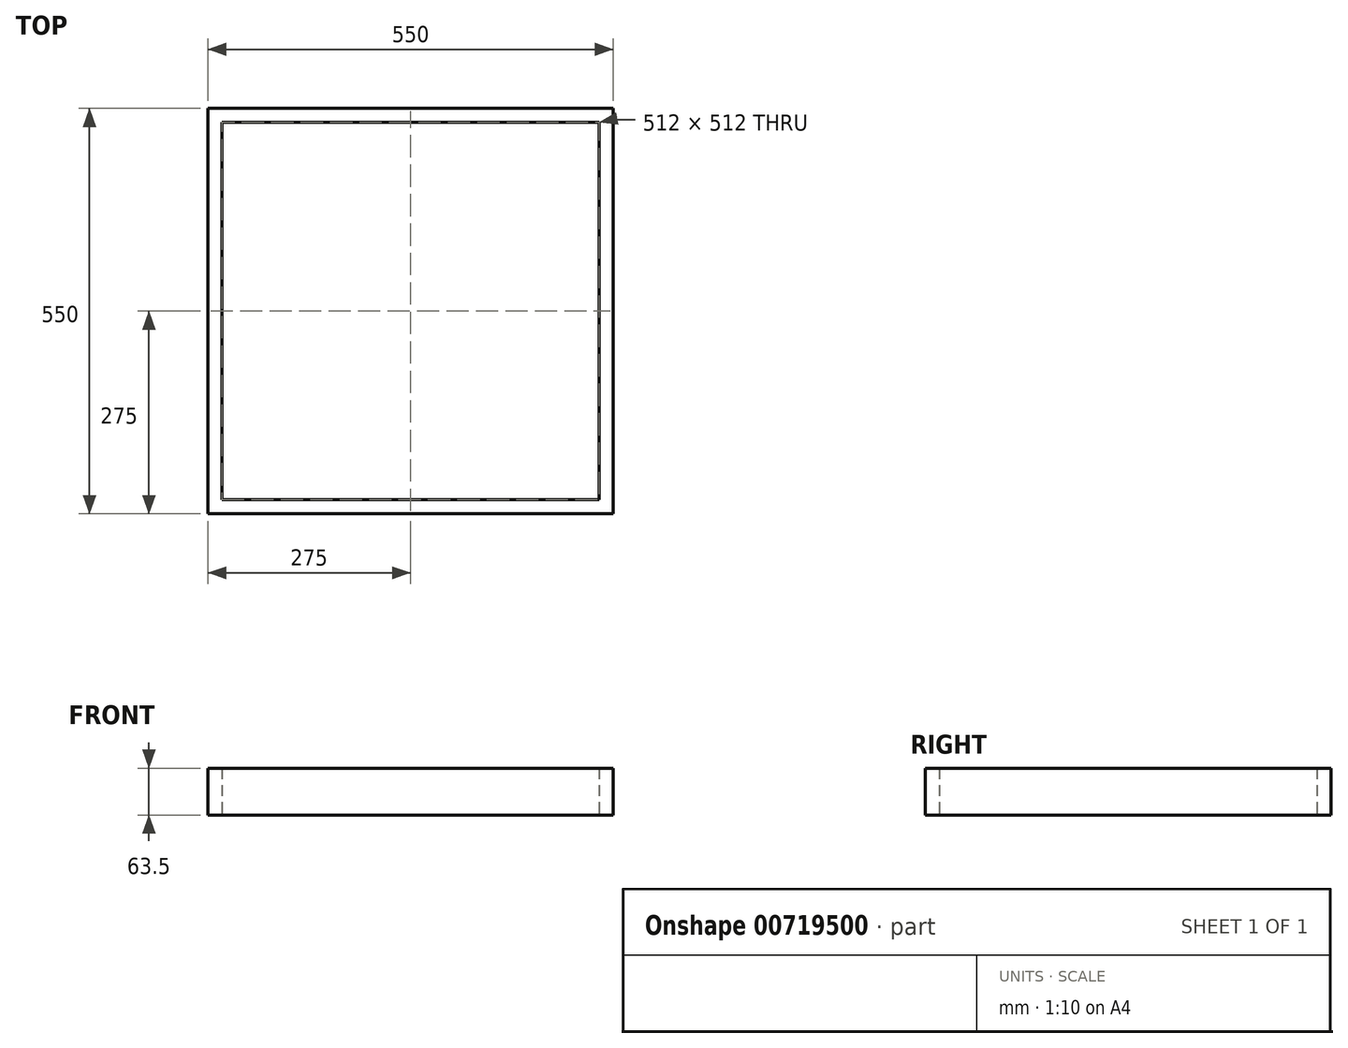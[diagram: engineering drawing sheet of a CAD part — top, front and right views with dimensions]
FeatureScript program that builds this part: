
annotation { "Feature Type Name" : "Feature", "Feature Type Description" : "" }
export const myFeature = defineFeature(function(context is Context, id is Id, definition is map)
    precondition{}
    {
        {
            var Q0;
            Q0=qCreatedBy(makeId("Top.planeOp"),FACE);
            var sketch = newSketch(context, id + "F0", { "sketchPlane" : qUnion([Q0])});
            skLineSegment(sketch, "E0.bottom", {"start": v(275, -275) * mm, "end": v(-275, -275) * mm});
            skLineSegment(sketch, "E0.top", {"start": v(275, 275) * mm, "end": v(-275, 275) * mm});
            skLineSegment(sketch, "E0.left", {"start": v(275, -275) * mm, "end": v(275, 275) * mm});
            skLineSegment(sketch, "E0.right", {"start": v(-275, -275) * mm, "end": v(-275, 275) * mm});
            skPoint(sketch, "E0.middle", {"position": v(0, 0) * mm});
            skLineSegment(sketch, "E1.bottom", {"start": v(256, -256) * mm, "end": v(-256, -256) * mm});
            skLineSegment(sketch, "E1.top", {"start": v(256, 256) * mm, "end": v(-256, 256) * mm});
            skLineSegment(sketch, "E1.left", {"start": v(256, -256) * mm, "end": v(256, 256) * mm});
            skLineSegment(sketch, "E1.right", {"start": v(-256, -256) * mm, "end": v(-256, 256) * mm});
            skSolve(sketch);
        }
        {
            var Q0;
            Q0=makeQuery(id+"F0.imprint","IMPRINT",FACE,{"disambiguationData":[TD([[makeQuery(id+"F0.imprint","IMPRINT",EDGE,{"derivedFrom":sQuery(id+"F0.wireOp",EDGE,"E0.bottom")}),-1.0]])]});
            extrude(context, id + "F1", {"entities" : qUnion([Q0]), "depth" : 63.5 * mm, "offsetDistance" : 25 * mm});
        }
    });
